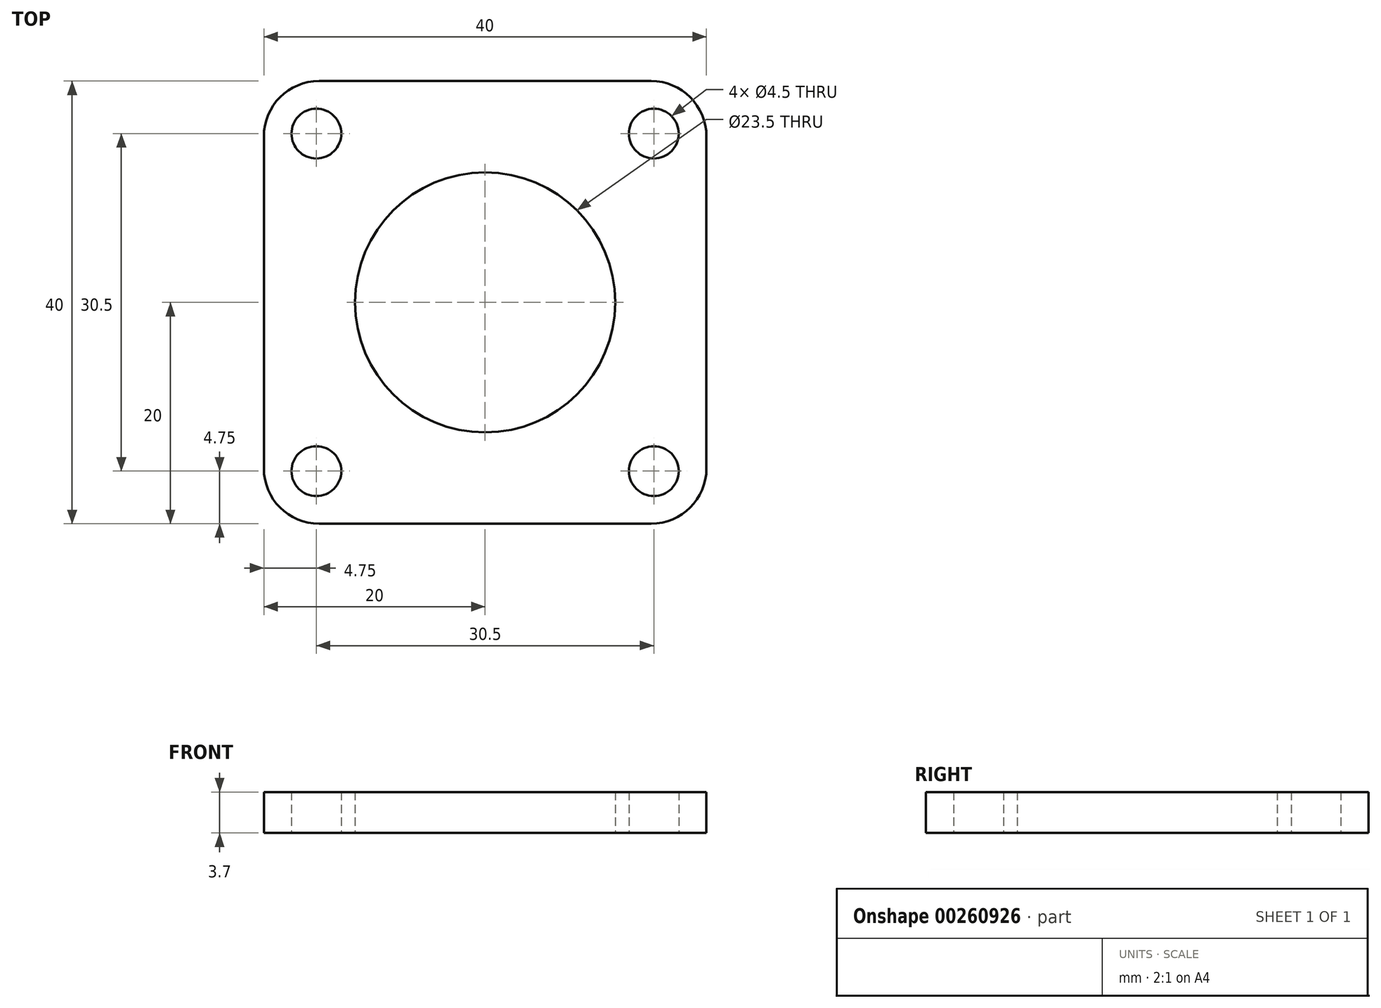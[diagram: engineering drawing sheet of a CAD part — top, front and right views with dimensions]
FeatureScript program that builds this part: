
annotation { "Feature Type Name" : "Feature", "Feature Type Description" : "" }
export const myFeature = defineFeature(function(context is Context, id is Id, definition is map)
    precondition{}
    {
        {
            var Q0;
            Q0=qCreatedBy(makeId("Top.planeOp"),FACE);
            var sketch = newSketch(context, id + "F0", { "sketchPlane" : qUnion([Q0])});
            skLineSegment(sketch, "E0.bottom", {"start": v(20, -20) * mm, "end": v(-20, -20) * mm});
            skLineSegment(sketch, "E0.top", {"start": v(20, 20) * mm, "end": v(-20, 20) * mm});
            skLineSegment(sketch, "E0.left", {"start": v(20, -20) * mm, "end": v(20, 20) * mm});
            skLineSegment(sketch, "E0.right", {"start": v(-20, -20) * mm, "end": v(-20, 20) * mm});
            skPoint(sketch, "E0.middle", {"position": v(0, 0) * mm});
            skCircle(sketch, "E1", {"center": v(-15.25, 15.25) * mm, "radius": 2.25 * mm});
            skCircle(sketch, "E2.0.1.0", {"center": v(-15.25, -15.25) * mm, "radius": 2.25 * mm});
            skCircle(sketch, "E2.1.0.0", {"center": v(15.25, 15.25) * mm, "radius": 2.25 * mm});
            skCircle(sketch, "E2.1.1.0", {"center": v(15.25, -15.25) * mm, "radius": 2.25 * mm});
            skLineSegment(sketch, "E2.direction1", {"start": v(-15.25, 15.25) * mm, "end": v(15.25, 15.25) * mm, "construction": true});
            skLineSegment(sketch, "E2.direction2", {"start": v(-15.25, 15.25) * mm, "end": v(-15.25, -15.25) * mm, "construction": true});
            skLineSegment(sketch, "E3", {"start": v(-15.25, 15.25) * mm, "end": v(0, 0) * mm, "construction": true});
            skLineSegment(sketch, "E4", {"start": v(0, 0) * mm, "end": v(-15.25, -15.25) * mm, "construction": true});
            skLineSegment(sketch, "E5", {"start": v(0, 0) * mm, "end": v(15.25, -15.25) * mm, "construction": true});
            skCircle(sketch, "E6", {"center": v(0, 0) * mm, "radius": 11.75 * mm});
            skSolve(sketch);
        }
        {
            var Q0;
            Q0=makeQuery(id+"F0.imprint","IMPRINT",FACE,{"disambiguationData":[TD([[makeQuery(id+"F0.imprint","IMPRINT",EDGE,{"derivedFrom":sQuery(id+"F0.wireOp",EDGE,"E0.bottom")}),-1.0]])]});
            extrude(context, id + "F1", {"entities" : qUnion([Q0]), "depth" : 3.7 * mm});
        }
        {
            var Q0;
            Q0=makeQuery(id+"F1.opExtrude","SWEPT_EDGE",EDGE,{"disambiguationData":[OSD([sQuery(id+"F0.wireOp",EDGE,"E0.bottom"),sQuery(id+"F0.wireOp",EDGE,"E0.left")])]});
            var Q1;
            Q1=makeQuery(id+"F1.opExtrude","SWEPT_EDGE",EDGE,{"disambiguationData":[OSD([sQuery(id+"F0.wireOp",EDGE,"E0.bottom"),sQuery(id+"F0.wireOp",EDGE,"E0.right")])]});
            var Q2;
            Q2=makeQuery(id+"F1.opExtrude","SWEPT_EDGE",EDGE,{"disambiguationData":[OSD([sQuery(id+"F0.wireOp",EDGE,"E0.top"),sQuery(id+"F0.wireOp",EDGE,"E0.left")])]});
            var Q3;
            Q3=makeQuery(id+"F1.opExtrude","SWEPT_EDGE",EDGE,{"disambiguationData":[OSD([sQuery(id+"F0.wireOp",EDGE,"E0.top"),sQuery(id+"F0.wireOp",EDGE,"E0.right")])]});
            fillet(context, id + "F2", {"entities" : qUnion([Q0, Q1, Q2, Q3]), "radius" : 5 * mm, "tangentPropagation" : true, "allowEdgeOverflow" : false});
        }
    });
